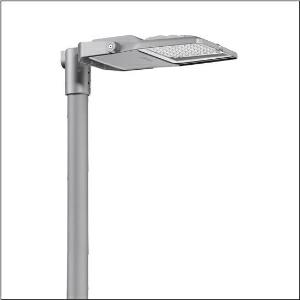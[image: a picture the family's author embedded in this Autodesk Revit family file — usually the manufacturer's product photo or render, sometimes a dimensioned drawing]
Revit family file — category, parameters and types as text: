
# Revit family: floodlight_fl_21_iq_mini___pl61_5xa7771b2c3a_a4a3
name_source: partatom
category: Lighting Fixtures
units: mm (PartAtom-declared; Revit-internal decimal feet)

## family parameters
Cut with Voids When Loaded = No
Host = Face
Light Source = No
Part Type = Normal
Room Calculation Point = No
Round Connector Dimension = Use Diameter
Shared = No

## types (1)
- --- (1 x LED, 6120 lm, 45.5 W, 3000K)
    Apparent Load = 46 VA
    CIE Flux Codes = 33 65 98 100 100
    Color Rendering = 70
    Color Temperature = 3000K
    Default Elevation = 1800 mm
    Description = Floodlight FL 21 iQ mini, floodlight, primary light control with lens, of PMMA, primary optical cover: protective disc, of toughened safety glass, transparent, light distribution: PL61, light emission: direct distribution, installation type: surface-mounted, LED, High Power LED, rated luminous flux: 6.120lm, luminous efficacy: 135lm/W, light colour: 730, colour temperature: 3000K, control: Auto-Match, Temp-Guard, Lumen-Switch, Night-Set, Smart-Wire, Light-Fading, Desk-Remote (wireless, voltage-free reading and setting of iQ features in the workshop via application-optimized NFC function/RFID function), optimised constant luminous flux control (CLO 2.0), with terminal, 6-pole, mains connection: 220..240V, AC, 50/60Hz, start of lifetime: 46W, end of service life: 48W, reduction: 22W, luminaire housing, of diecast aluminium, powder-coated, Siteco® metallic grey (DB 702S), corrosivity category C5 mid according to DIN EN ISO 12944, sealing non-destructively replaceable, please order mast flange separately, mast bracket, of steel, galvanised, powder-coated, Siteco® metallic grey (DB 702S), protection rating (complete): IP66, insulation class (complete): insulation class II (safety insulation), certification: CE, ENEC, VDE, protection symbol: D, impact resistance: IK08, permissible operating ambient temperature: -40..+40°C, permissible operating ambient temperature for outdoor applications: -40..+50°C, standard: DIN EN 12944, LABS conformity tested according to VDMA 24364:2018-05, packaging unit: 1 piece

Light Distribution: PL61
    Height = 70 mm
    Lamp = 1 x LED
    Lamp Light Flux = 6120 lm
    Lamp Power = 45.5 W
    Lamp count = 1
    Length = 485 mm
    Luminous efficacy = 135 lm/W
    Manufacturer = Siteco
    ModVariant = No
    Model = 5XA7771B2C3A
    Number of Poles = 1
    OnlyDefault = Yes
    Power Factor = 1
    Product Name = Floodlight FL 21 iQ mini | PL61
    Product group = floodlight | pylon annexe
    ProductGroupID = 6200
    Protection Class = Protection class II
    Protection Degree = IP 66
    RLX_Detail_Level = 1
    RLX_Emergency_Light_Flux = 0 lm
    RLX_Emergency_Type = 0
    RLX_Emergency_Type_DB = No
    RlxData = <blob elided: 101201 chars, md5=dc7ce00e>
    Socket = socket
    Standby Power = 0 W
    System Light Flux = 6120 lm
    System Power = 46 W
    Type Comments = factory setting: luminous flux: 100 % | dim-lin: 254 | 463 mA
    Type Image = l_1007125.jpg
    URL = http://relux.com
    VarID = @adj_106911
    Voltage = 0 V
    Weight = 0.00 kg
    Width = 337 mm

## geometry (parser evidence)
native form markers: Blend x4, Sweep x12
no freeform markers — native parametric forms only
